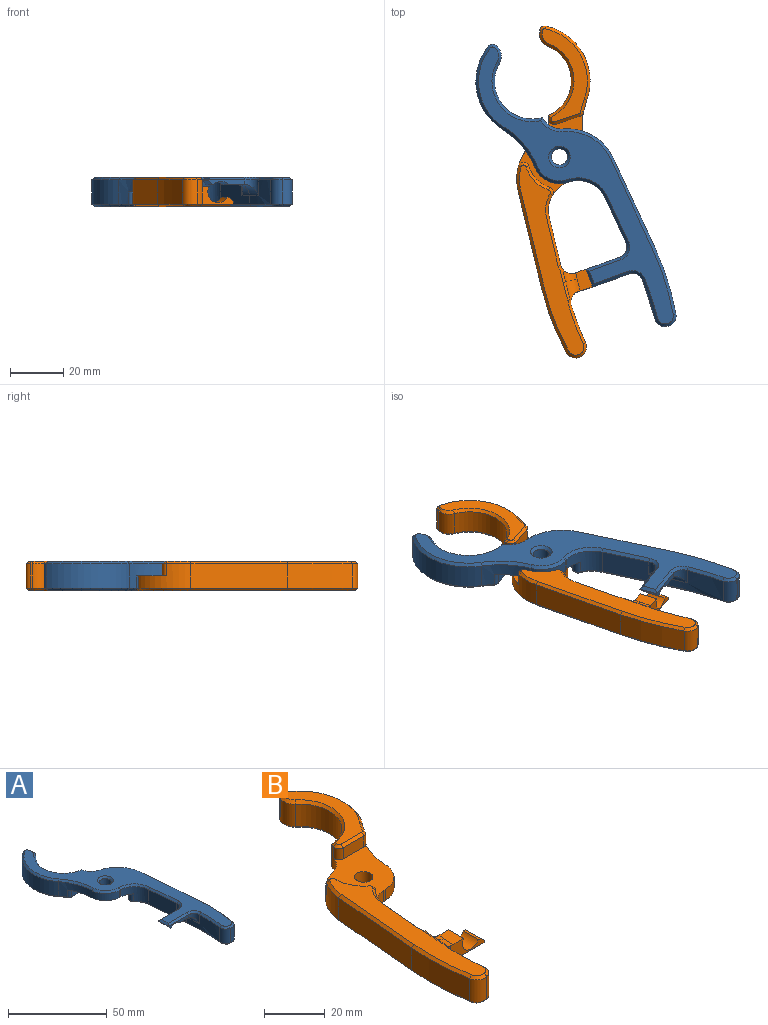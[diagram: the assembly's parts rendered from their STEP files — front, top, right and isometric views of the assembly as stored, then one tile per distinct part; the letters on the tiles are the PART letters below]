
ASSEMBLY  parts=2 mates=1
PART A: 88 faces, bbox 43.3x121.7x11 mm
  f0: cylinder r=21mm len=31.04mm, axis (0,0,-1), area 321.2mm2, adj f21,f28,f67,f81
  f1: plane 34.28x18.42mm, normal (0,0,-1), area 207.4mm2, adj f78,f79,f80,f81,f82,f83,f84,f85
  f2: cylinder r=130mm len=24.03mm, axis (0,0,-1), area 165.7mm2, adj f12,f32,f34,f35,f49,f62
  f3: plane 9x0.06mm, normal (-0.21,-0.98,0), area 0.6mm2, adj f35,f36,f45,f66
  f4: cylinder r=100mm len=25.91mm, axis (0,0,-1), area 234.1mm2, adj f5,f36,f41,f70
  f5: plane 37.07x9mm, normal (1,0.09,0), area 334.9mm2, adj f4,f6,f42,f72
  f6: cylinder r=18.78mm len=16.5mm, axis (0,0,-1), area 145.2mm2, adj f5,f15,f19,f37,f44,f74
  f7: cylinder r=14mm len=24.65mm, axis (0,0,-1), area 298.3mm2, adj f20,f37,f75,f82
  f8: plane 9x0.51mm, normal (0.91,0.42,0), area 5.1mm2, adj f20,f28,f71,f78
  f9: cylinder r=10mm len=9.99mm, axis (0,0,-1), area 68.8mm2, adj f10,f15,f21,f63
  f10: plane 4.5x0.81mm, normal (-0.09,-1,0), area 3.6mm2, adj f9,f15,f29,f61
  f11: cylinder r=3.05mm len=6.1mm, axis (0,0,-1), area 86.2mm2, adj f15,f77
  f12: plane 24.93x9mm, normal (-1,-0.09,0), area 188.9mm2, adj f2,f29,f31,f33,f51,f57
  f13: plane 119.72x41.33mm, normal (0,0,1), area 1167.3mm2, adj f54,f55,f56,f57,f58,f59,f60,f61
  f14: plane 73.91x13.96mm, normal (0,0,-1), area 497.3mm2, adj f41,f42,f43,f44,f45,f46,f47,f48
  f15: plane 29.48x27.35mm, normal (0,0,-1), area 409mm2, adj f6,f9,f10,f11,f16,f17,f18,f19
  f16: plane 9.49x4.5mm, normal (0,-1,0), area 42.7mm2, adj f15,f38,f40,f87
  f17: cylinder r=12mm len=9.62mm, axis (0,0,1), area 50.2mm2, adj f15,f18,f39,f50
  f18: plane 4.5x0.47mm, normal (-1,0,0), area 2.1mm2, adj f15,f17,f19,f48
  f19: cylinder r=2mm len=4.5mm, axis (0,0,-1), area 23mm2, adj f6,f15,f18,f46
  f20: cylinder r=5mm len=9mm, axis (0,0,-1), area 58.7mm2, adj f7,f8,f73,f80
  f21: cylinder r=30mm len=17.37mm, axis (0,0,1), area 106.2mm2, adj f0,f9,f15,f40,f65,f83
  f22: plane 7.02x6.46mm, normal (0,0,-1), area 43.6mm2, adj f23,f26,f27,f31,f33,f34
  f23: plane 14.46x1.7mm, normal (0,-1,0), area 18.7mm2, adj f22,f24,f25,f26,f30,f32,f34,f58
  f24: plane 7x0.2mm, normal (-1,0,0), area 1.4mm2, adj f23,f27,f30,f56
  f25: plane 7x0.64mm, normal (0,0,-1), area 4.5mm2, adj f23,f26,f27,f30
  f26: cylinder r=4mm len=7mm, axis (0,-1,0), area 44.5mm2, adj f22,f23,f25,f27
  f27: plane 13.45x1.7mm, normal (0,1,0), area 17mm2, adj f22,f24,f25,f26,f30,f31,f54
  f28: cylinder r=2mm len=9mm, axis (0,0,-1), area 30.2mm2, adj f0,f8,f69,f79
  f29: cylinder r=11mm len=10mm, axis (0,0,-1), area 107.1mm2, adj f10,f12,f15,f39,f53,f59
  f30: plane 7x1.5mm, normal (-0.71,0,-0.71), area 14.8mm2, adj f23,f24,f25,f27
  f31: cylinder r=4mm len=5.7mm, axis (0,0,1), area 20.4mm2, adj f12,f22,f27,f33,f55
  f32: cylinder r=4mm len=5.7mm, axis (0,0,-1), area 19.8mm2, adj f2,f23,f34,f60
  f33: cylinder r=4mm len=6.7mm, axis (-0.09,1,0), area 24mm2, adj f12,f22,f31,f34
  f34: torus R=126mm, axis (0,0,-1), area 39.4mm2, adj f2,f22,f23,f32,f33
  f35: cylinder r=4mm len=9mm, axis (0,0,-1), area 52.4mm2, adj f2,f3,f47,f64
  f36: cylinder r=4mm len=9mm, axis (0,0,-1), area 58mm2, adj f3,f4,f43,f68
  f37: cylinder r=8mm len=9mm, axis (0,0,1), area 48.9mm2, adj f6,f7,f15,f38,f76,f84
  f38: cylinder r=2mm len=4.5mm, axis (0,0,1), area 17mm2, adj f15,f16,f37,f86
  f39: cylinder r=2mm len=4.5mm, axis (0,0,1), area 16.1mm2, adj f15,f17,f29,f52
  f40: cylinder r=2mm len=4.5mm, axis (0,0,1), area 9.5mm2, adj f15,f16,f21,f85
  f41: cone r=99mm half-angle=45deg, axis (0,0,1), area 36.6mm2, adj f4,f14,f42,f43
  f42: plane 37.16x4.24mm, normal (0.7,0.06,-0.71), area 52.6mm2, adj f5,f14,f41,f44
  f43: cone r=3mm half-angle=45deg, axis (0,0,1), area 8mm2, adj f14,f36,f41,f45
  f44: cone r=17.78mm half-angle=45deg, axis (0,0,1), area 12.8mm2, adj f6,f14,f42,f46
  f45: plane 1x0.99mm, normal (-0.15,-0.69,-0.71), area 0.1mm2, adj f3,f14,f43,f47
  f46: cone r=1mm half-angle=45deg, axis (0,0,1), area 5.4mm2, adj f14,f19,f44,f48
  f47: cone r=3mm half-angle=45deg, axis (0,0,1), area 7.2mm2, adj f14,f35,f45,f49
  f48: plane 1x1mm, normal (-0.71,0,-0.71), area 0.7mm2, adj f14,f18,f46,f50
  f49: cone r=130mm half-angle=45deg, axis (0,0,-1), area 34.2mm2, adj f2,f14,f47,f51
  f50: cone r=13mm half-angle=45deg, axis (0,0,-1), area 16.4mm2, adj f14,f17,f48,f52
  f51: plane 25.02x3.18mm, normal (-0.7,-0.06,-0.71), area 35.4mm2, adj f12,f14,f49,f53
  f52: cone r=1mm half-angle=45deg, axis (0,0,1), area 3.8mm2, adj f14,f39,f50,f53
  f53: cone r=12mm half-angle=45deg, axis (0,0,-1), area 12.5mm2, adj f14,f29,f51,f52
  f54: plane 13.45x1mm, normal (0,0.71,0.71), area 18.3mm2, adj f13,f27,f55,f56
  f55: cone r=5mm half-angle=45deg, axis (0,0,1), area 10.6mm2, adj f13,f31,f54,f57
  f56: plane 7x1mm, normal (-0.71,0,0.71), area 8.5mm2, adj f13,f24,f54,f58
  f57: plane 18.67x2.62mm, normal (-0.7,-0.06,0.71), area 26.4mm2, adj f12,f13,f55,f59
  f58: plane 14.46x1mm, normal (0,-0.71,0.71), area 19.7mm2, adj f13,f23,f56,f60
  f59: cone r=12mm half-angle=45deg, axis (0,0,1), area 22.7mm2, adj f13,f29,f57,f61
  f60: cone r=5mm half-angle=45deg, axis (0,0,1), area 9.9mm2, adj f13,f32,f58,f62
  f61: plane 1.07x1mm, normal (-0.06,-0.7,0.71), area 1.2mm2, adj f10,f13,f59,f63
  f62: cone r=131mm half-angle=45deg, axis (0,0,1), area 21.5mm2, adj f2,f13,f60,f64
  f63: cone r=10mm half-angle=45deg, axis (0,0,-1), area 20.6mm2, adj f9,f13,f61,f65
  f64: cone r=3mm half-angle=45deg, axis (0,0,-1), area 7.2mm2, adj f13,f35,f62,f66
  f65: cone r=31mm half-angle=45deg, axis (0,0,1), area 27.1mm2, adj f13,f21,f63,f67
  f66: plane 1x0.99mm, normal (-0.15,-0.69,0.71), area 0.1mm2, adj f3,f13,f64,f68
  f67: cone r=21mm half-angle=45deg, axis (0,0,-1), area 49.3mm2, adj f0,f13,f65,f69
  f68: cone r=3mm half-angle=45deg, axis (0,0,-1), area 8mm2, adj f13,f36,f66,f70
  f69: cone r=1mm half-angle=45deg, axis (0,0,-1), area 3.6mm2, adj f13,f28,f67,f71
  f70: cone r=100mm half-angle=45deg, axis (0,0,-1), area 36.6mm2, adj f4,f13,f68,f72
  f71: plane 1.14x1mm, normal (0.64,0.3,0.71), area 0.8mm2, adj f8,f13,f69,f73
  f72: plane 37.16x4.24mm, normal (0.7,0.06,0.71), area 52.6mm2, adj f5,f13,f70,f74
  f73: cone r=4mm half-angle=45deg, axis (0,0,-1), area 8.3mm2, adj f13,f20,f71,f75
  f74: cone r=18.78mm half-angle=45deg, axis (0,0,-1), area 31.6mm2, adj f6,f13,f72,f76
  f75: cone r=15mm half-angle=45deg, axis (0,0,1), area 48mm2, adj f7,f13,f73,f76
  f76: cone r=9mm half-angle=45deg, axis (0,0,1), area 13.6mm2, adj f13,f37,f74,f75
  f77: cone r=4.05mm half-angle=45deg, axis (0,0,1), area 31.5mm2, adj f11,f13
  f78: plane 1.14x1mm, normal (0.64,0.3,-0.71), area 0.8mm2, adj f1,f8,f79,f80
  f79: cone r=1mm half-angle=45deg, axis (0,0,1), area 3.6mm2, adj f1,f28,f78,f81
  f80: cone r=4mm half-angle=45deg, axis (0,0,1), area 8.3mm2, adj f1,f20,f78,f82
  f81: cone r=20mm half-angle=45deg, axis (0,0,1), area 49.3mm2, adj f0,f1,f79,f83
  f82: cone r=14mm half-angle=45deg, axis (0,0,-1), area 48mm2, adj f1,f7,f80,f84
  f83: cone r=31mm half-angle=45deg, axis (0,0,-1), area 6.8mm2, adj f1,f21,f81,f85
  f84: cone r=9mm half-angle=45deg, axis (0,0,-1), area 1.6mm2, adj f1,f37,f82,f86
  f85: cone r=1mm half-angle=45deg, axis (0,0,1), area 2.2mm2, adj f1,f40,f83,f87
  f86: cone r=1mm half-angle=45deg, axis (0,0,1), area 4mm2, adj f1,f38,f84,f87
  f87: plane 9.49x1mm, normal (0,-0.71,-0.71), area 13.4mm2, adj f1,f16,f85,f86
PART B: 92 faces, bbox 43.3x121.7x12.5 mm
  f0: cylinder r=130mm len=15.11mm, axis (0,0,-1), area 136.2mm2, adj f32,f36,f42,f66
  f1: plane 18.58x9mm, normal (1,-0.09,0), area 167.9mm2, adj f29,f31,f52,f61
  f2: plane 4.5x0.81mm, normal (0.09,-1,0), area 3.6mm2, adj f3,f18,f29,f65
  f3: cylinder r=10mm len=9.99mm, axis (0,0,-1), area 68.8mm2, adj f2,f18,f21,f67
  f4: cylinder r=21mm len=31.04mm, axis (0,0,-1), area 321.2mm2, adj f21,f28,f71,f86
  f5: cylinder r=18.78mm len=16.5mm, axis (0,0,-1), area 145.2mm2, adj f11,f18,f19,f37,f51,f78
  f6: cylinder r=3.05mm len=6.1mm, axis (0,0,-1), area 86.2mm2, adj f18,f81
  f7: plane 34.28x18.42mm, normal (0,0,1), area 207.4mm2, adj f82,f83,f84,f85,f86,f87,f88,f89
  f8: plane 73.91x13.96mm, normal (0,0,1), area 501.4mm2, adj f41,f42,f43,f44,f45,f46,f47,f48
  f9: plane 9x0.51mm, normal (-0.91,0.42,0), area 5.1mm2, adj f20,f28,f75,f82
  f10: cylinder r=14mm len=24.65mm, axis (0,0,-1), area 298.3mm2, adj f20,f37,f79,f85
  f11: plane 37.07x9mm, normal (-1,0.09,0), area 334.9mm2, adj f5,f12,f49,f76
  f12: cylinder r=100mm len=25.91mm, axis (0,0,-1), area 234.1mm2, adj f11,f35,f47,f74
  f13: plane 9x0.06mm, normal (0.21,-0.98,0), area 0.6mm2, adj f35,f36,f43,f70
  f14: plane 119.72x41.33mm, normal (0,0,-1), area 1172.3mm2, adj f58,f59,f60,f61,f62,f63,f64,f65
  f15: plane 9.49x4.5mm, normal (0,-1,0), area 42.7mm2, adj f18,f38,f40,f91
  f16: plane 4.5x0.47mm, normal (1,0,0), area 2.1mm2, adj f17,f18,f19,f55
  f17: cylinder r=12mm len=9.62mm, axis (0,0,1), area 50.2mm2, adj f16,f18,f39,f57
  f18: plane 29.48x27.35mm, normal (0,0,1), area 409mm2, adj f2,f3,f5,f6,f15,f16,f17,f19
  f19: cylinder r=2mm len=4.5mm, axis (0,0,-1), area 23mm2, adj f5,f16,f18,f53
  f20: cylinder r=5mm len=9mm, axis (0,0,-1), area 58.7mm2, adj f9,f10,f77,f83
  f21: cylinder r=30mm len=17.37mm, axis (0,0,1), area 106.2mm2, adj f3,f4,f18,f40,f69,f88
  f22: plane 14.45x6.52mm, normal (0,1,0), area 43.6mm2, adj f23,f24,f25,f26,f30,f31,f34,f58
  f23: plane 7x5.09mm, normal (0,0,1), area 33.9mm2, adj f22,f26,f27,f33,f34
  f24: plane 7x1mm, normal (1,0,0), area 7mm2, adj f22,f27,f30,f60
  f25: plane 7x1.04mm, normal (0,0,1), area 7.3mm2, adj f22,f26,f27,f30
  f26: cylinder r=4mm len=7.46mm, axis (0,-1,0), area 88mm2, adj f22,f23,f25,f27
  f27: plane 15.46x6.58mm, normal (0,-1,0), area 50.2mm2, adj f23,f24,f25,f26,f30,f32,f33,f62
  f28: cylinder r=2mm len=9mm, axis (0,0,-1), area 30.2mm2, adj f4,f9,f73,f84
  f29: cylinder r=11mm len=10mm, axis (0,0,-1), area 107.1mm2, adj f1,f2,f18,f39,f54,f63
  f30: plane 7x1.5mm, normal (0.71,0,0.71), area 14.8mm2, adj f22,f24,f25,f27
  f31: cylinder r=4mm len=9mm, axis (0,0,-1), area 52.4mm2, adj f1,f22,f34,f50,f59
  f32: cylinder r=4mm len=9mm, axis (0,0,-1), area 49.7mm2, adj f0,f27,f33,f44,f64
  f33: torus R=125.23mm, axis (0,0,1), area 31.4mm2, adj f23,f27,f32,f34,f44,f46
  f34: cylinder r=5mm len=4.93mm, axis (0.09,1,0), area 17.8mm2, adj f22,f23,f31,f33,f48,f50
  f35: cylinder r=4mm len=9mm, axis (0,0,-1), area 58mm2, adj f12,f13,f45,f72
  f36: cylinder r=4mm len=9mm, axis (0,0,-1), area 52.4mm2, adj f0,f13,f41,f68
  f37: cylinder r=8mm len=9mm, axis (0,0,1), area 48.9mm2, adj f5,f10,f18,f38,f80,f87
  f38: cylinder r=2mm len=4.5mm, axis (0,0,1), area 17mm2, adj f15,f18,f37,f89
  f39: cylinder r=2mm len=4.5mm, axis (0,0,-1), area 16.1mm2, adj f17,f18,f29,f56
  f40: cylinder r=2mm len=4.5mm, axis (0,0,1), area 9.5mm2, adj f15,f18,f21,f90
  f41: cone r=3mm half-angle=45deg, axis (0,0,-1), area 7.2mm2, adj f8,f36,f42,f43
  f42: cone r=130mm half-angle=45deg, axis (0,0,1), area 21.5mm2, adj f0,f8,f41,f44
  f43: plane 1x0.99mm, normal (0.15,-0.69,0.71), area 0.1mm2, adj f8,f13,f41,f45
  f44: cone r=4mm half-angle=45deg, axis (0,0,1), area 3.1mm2, adj f8,f32,f33,f42,f46
  f45: cone r=3mm half-angle=45deg, axis (0,0,-1), area 8mm2, adj f8,f35,f43,f47
  f46: cone r=129.78mm half-angle=57.3deg, axis (0,0,1), area 7.4mm2, adj f8,f33,f44,f48
  f47: cone r=99mm half-angle=45deg, axis (0,0,-1), area 36.6mm2, adj f8,f12,f45,f49
  f48: plane 4.69x1.26mm, normal (0.54,-0.05,0.84), area 4.7mm2, adj f8,f34,f46,f50
  f49: plane 37.16x4.24mm, normal (-0.7,0.06,0.71), area 52.6mm2, adj f8,f11,f47,f51
  f50: cone r=5mm half-angle=45deg, axis (0,0,1), area 3mm2, adj f8,f31,f34,f48,f52
  f51: cone r=17.78mm half-angle=45deg, axis (0,0,-1), area 12.8mm2, adj f5,f8,f49,f53
  f52: plane 18.67x2.62mm, normal (0.7,-0.06,0.71), area 26.4mm2, adj f1,f8,f50,f54
  f53: cone r=1mm half-angle=45deg, axis (0,0,-1), area 5.4mm2, adj f8,f19,f51,f55
  f54: cone r=12mm half-angle=45deg, axis (0,0,1), area 12.5mm2, adj f8,f29,f52,f56
  f55: plane 1x1mm, normal (0.71,0,0.71), area 0.7mm2, adj f8,f16,f53,f57
  f56: cone r=1mm half-angle=45deg, axis (0,0,-1), area 3.8mm2, adj f8,f39,f54,f57
  f57: cone r=12mm half-angle=45deg, axis (0,0,1), area 16.4mm2, adj f8,f17,f55,f56
  f58: plane 14.45x1mm, normal (0,0.71,-0.71), area 19.7mm2, adj f14,f22,f59,f60
  f59: cone r=5mm half-angle=45deg, axis (0,0,-1), area 10.6mm2, adj f14,f31,f58,f61
  f60: plane 7x1mm, normal (0.71,0,-0.71), area 8.5mm2, adj f14,f24,f58,f62
  f61: plane 18.67x2.62mm, normal (0.7,-0.06,-0.71), area 26.4mm2, adj f1,f14,f59,f63
  f62: plane 15.46x1mm, normal (0,-0.71,-0.71), area 21.2mm2, adj f14,f27,f60,f64
  f63: cone r=12mm half-angle=45deg, axis (0,0,-1), area 22.7mm2, adj f14,f29,f61,f65
  f64: cone r=5mm half-angle=45deg, axis (0,0,-1), area 9.9mm2, adj f14,f32,f62,f66
  f65: plane 1.07x1mm, normal (0.06,-0.7,-0.71), area 1.2mm2, adj f2,f14,f63,f67
  f66: cone r=131mm half-angle=45deg, axis (0,0,-1), area 21.5mm2, adj f0,f14,f64,f68
  f67: cone r=10mm half-angle=45deg, axis (0,0,1), area 20.6mm2, adj f3,f14,f65,f69
  f68: cone r=3mm half-angle=45deg, axis (0,0,1), area 7.2mm2, adj f14,f36,f66,f70
  f69: cone r=31mm half-angle=45deg, axis (0,0,-1), area 27.1mm2, adj f14,f21,f67,f71
  f70: plane 1x0.99mm, normal (0.15,-0.69,-0.71), area 0.1mm2, adj f13,f14,f68,f72
  f71: cone r=21mm half-angle=45deg, axis (0,0,1), area 49.3mm2, adj f4,f14,f69,f73
  f72: cone r=3mm half-angle=45deg, axis (0,0,1), area 8mm2, adj f14,f35,f70,f74
  f73: cone r=1mm half-angle=45deg, axis (0,0,1), area 3.6mm2, adj f14,f28,f71,f75
  f74: cone r=100mm half-angle=45deg, axis (0,0,1), area 36.6mm2, adj f12,f14,f72,f76
  f75: plane 1.14x1mm, normal (-0.64,0.3,-0.71), area 0.8mm2, adj f9,f14,f73,f77
  f76: plane 37.16x4.24mm, normal (-0.7,0.06,-0.71), area 52.6mm2, adj f11,f14,f74,f78
  f77: cone r=4mm half-angle=45deg, axis (0,0,1), area 8.3mm2, adj f14,f20,f75,f79
  f78: cone r=18.78mm half-angle=45deg, axis (0,0,1), area 31.6mm2, adj f5,f14,f76,f80
  f79: cone r=15mm half-angle=45deg, axis (0,0,-1), area 48mm2, adj f10,f14,f77,f80
  f80: cone r=9mm half-angle=45deg, axis (0,0,-1), area 13.6mm2, adj f14,f37,f78,f79
  f81: cone r=4.05mm half-angle=45deg, axis (0,0,-1), area 31.5mm2, adj f6,f14
  f82: plane 1.14x1mm, normal (-0.64,0.3,0.71), area 0.8mm2, adj f7,f9,f83,f84
  f83: cone r=4mm half-angle=45deg, axis (0,0,-1), area 8.3mm2, adj f7,f20,f82,f85
  f84: cone r=1mm half-angle=45deg, axis (0,0,-1), area 3.6mm2, adj f7,f28,f82,f86
  f85: cone r=14mm half-angle=45deg, axis (0,0,1), area 48mm2, adj f7,f10,f83,f87
  f86: cone r=20mm half-angle=45deg, axis (0,0,-1), area 49.3mm2, adj f4,f7,f84,f88
  f87: cone r=9mm half-angle=45deg, axis (0,0,1), area 1.6mm2, adj f7,f37,f85,f89
  f88: cone r=31mm half-angle=45deg, axis (0,0,1), area 6.8mm2, adj f7,f21,f86,f90
  f89: cone r=1mm half-angle=45deg, axis (0,0,-1), area 4mm2, adj f7,f38,f87,f91
  f90: cone r=1mm half-angle=45deg, axis (0,0,-1), area 2.2mm2, adj f7,f40,f88,f91
  f91: plane 9.49x1mm, normal (0,-0.71,0.71), area 13.4mm2, adj f7,f15,f89,f90
PLACE A rot(axis=(0,0,1),20deg) t=(-20.33,49.02,6.85)mm
PLACE B rot(axis=(0,0,1),18.5deg) t=(-19.62,49.27,6.85)mm
MATE revolute B.f3 <-> A.f9  axis (0,0,1) through (-10.07,20.83,12.35)mm
